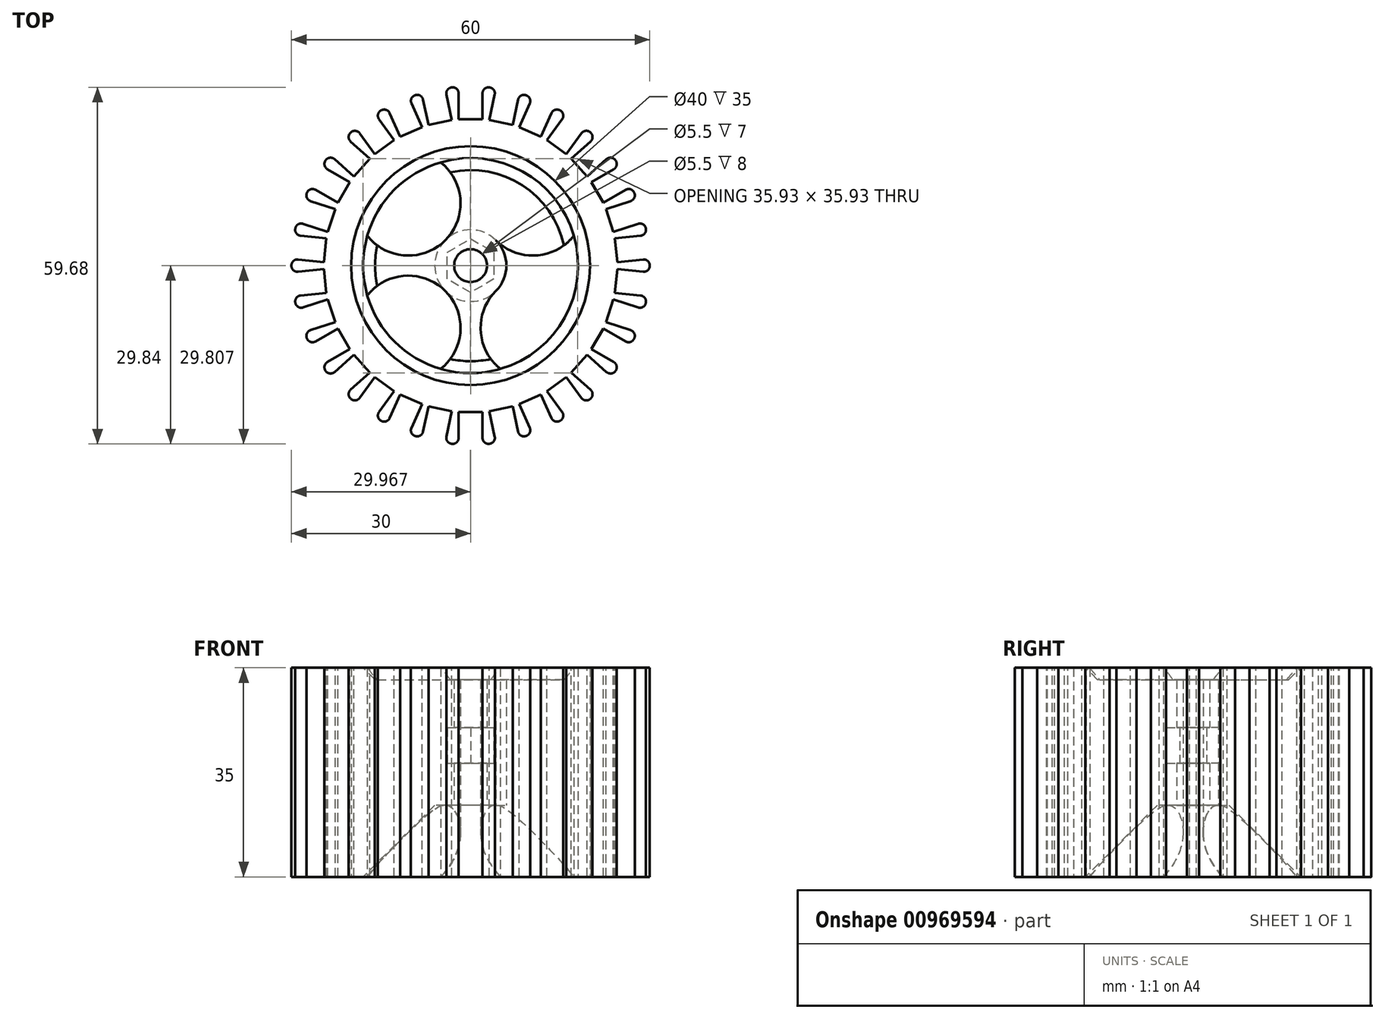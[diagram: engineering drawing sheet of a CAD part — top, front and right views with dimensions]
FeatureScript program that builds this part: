
annotation { "Feature Type Name" : "Feature", "Feature Type Description" : "" }
export const myFeature = defineFeature(function(context is Context, id is Id, definition is map)
    precondition{}
    {
        {
            var Q0;
            Q0=qCreatedBy(makeId("Top.planeOp"),FACE);
            var sketch = newSketch(context, id + "F0", { "sketchPlane" : qUnion([Q0])});
            skCircle(sketch, "E0", {"center": v(0, 0) * mm, "radius": 30 * mm});
            skCircle(sketch, "E1", {"center": v(0, 0) * mm, "radius": 20 * mm});
            skCircle(sketch, "E2", {"center": v(0, 0) * mm, "radius": 21 * mm});
            skCircle(sketch, "E3", {"center": v(0, 0) * mm, "radius": 18 * mm});
            skCircle(sketch, "E4", {"center": v(0, 0) * mm, "radius": 6 * mm});
            skArc(sketch, "E5", {"start": v(-17.3, 5) * mm, "mid": v(-4.24, 4.24) * mm, "end": v(-5, 17.3) * mm});
            skArc(sketch, "E6.MirrorCS", {"start": v(17.3, 5) * mm, "mid": v(4.24, 4.24) * mm, "end": v(5, 17.3) * mm});
            skArc(sketch, "E7.MirrorCS", {"start": v(-17.3, -5) * mm, "mid": v(-4.24, -4.24) * mm, "end": v(-5, -17.3) * mm});
            skArc(sketch, "E8.MirrorCS", {"start": v(17.3, -5) * mm, "mid": v(4.24, -4.24) * mm, "end": v(5, -17.3) * mm});
            skCircle(sketch, "E9.cCircle", {"center": v(0, 0) * mm, "radius": 3.9 * mm, "construction": true});
            skLineSegment(sketch, "E9.0", {"start": v(3.9, 2.25) * mm, "end": v(3.9, -2.25) * mm});
            skLineSegment(sketch, "E9.1", {"start": v(3.9, -2.25) * mm, "end": v(0, -4.5) * mm});
            skLineSegment(sketch, "E9.2", {"start": v(0, -4.5) * mm, "end": v(-3.9, -2.25) * mm});
            skLineSegment(sketch, "E9.3", {"start": v(-3.9, -2.25) * mm, "end": v(-3.9, 2.25) * mm});
            skLineSegment(sketch, "E9.4", {"start": v(-3.9, 2.25) * mm, "end": v(0, 4.5) * mm});
            skLineSegment(sketch, "E9.5", {"start": v(0, 4.5) * mm, "end": v(3.9, 2.25) * mm});
            skPoint(sketch, "E9.0.midPoint", {"position": v(3.9, 0) * mm});
            skCircle(sketch, "E10", {"center": v(0, 0) * mm, "radius": 3 * mm});
            skCircle(sketch, "E11", {"center": v(0, 0) * mm, "radius": 2.75 * mm});
            skSolve(sketch);
        }
        {
            var Q0;
            {var subQ0=sQuery(id+"F0.wireOp",EDGE,"E5");var subQ1=sQuery(id+"F0.wireOp",EDGE,"E3");var subQ2=makeQuery(id+"F0.imprint","INTERSECT",VERTEX,{"disambiguationData":[OD(1.0)],"derivedFrom":[subQ1,subQ0]});Q0=makeQuery(id+"F0.imprint","IMPRINT",FACE,{"disambiguationData":[TD([[makeQuery(id+"F0.imprint","IMPRINT",EDGE,{"disambiguationData":[TD([[subQ2,1.0]])],"derivedFrom":subQ1}),1.0]])]});}
            var Q1;
            {var subQ0=sQuery(id+"F0.wireOp",EDGE,"E5");var subQ1=sQuery(id+"F0.wireOp",EDGE,"E3");var subQ2=makeQuery(id+"F0.imprint","INTERSECT",VERTEX,{"disambiguationData":[OD(0.0)],"derivedFrom":[subQ1,subQ0]});Q1=makeQuery(id+"F0.imprint","IMPRINT",FACE,{"disambiguationData":[TD([[makeQuery(id+"F0.imprint","IMPRINT",EDGE,{"disambiguationData":[TD([[subQ2,-1.0]])],"derivedFrom":subQ1}),1.0]])]});}
            var Q2;
            {var subQ0=sQuery(id+"F0.wireOp",EDGE,"E7.MirrorCS");var subQ1=sQuery(id+"F0.wireOp",EDGE,"E3");var subQ2=makeQuery(id+"F0.imprint","INTERSECT",VERTEX,{"disambiguationData":[OD(1.0)],"derivedFrom":[subQ1,subQ0]});Q2=makeQuery(id+"F0.imprint","IMPRINT",FACE,{"disambiguationData":[TD([[makeQuery(id+"F0.imprint","IMPRINT",EDGE,{"disambiguationData":[TD([[subQ2,-1.0]])],"derivedFrom":subQ1}),1.0]])]});}
            var Q3;
            {var subQ0=sQuery(id+"F0.wireOp",EDGE,"E6.MirrorCS");var subQ1=sQuery(id+"F0.wireOp",EDGE,"E3");var subQ2=makeQuery(id+"F0.imprint","INTERSECT",VERTEX,{"disambiguationData":[OD(0.0)],"derivedFrom":[subQ1,subQ0]});Q3=makeQuery(id+"F0.imprint","IMPRINT",FACE,{"disambiguationData":[TD([[makeQuery(id+"F0.imprint","IMPRINT",EDGE,{"disambiguationData":[TD([[subQ2,1.0]])],"derivedFrom":subQ1}),1.0]])]});}
            var Q4;
            Q4=makeQuery(id+"F0.imprint","IMPRINT",FACE,{"disambiguationData":[TD([[makeQuery(id+"F0.imprint","IMPRINT",EDGE,{"derivedFrom":sQuery(id+"F0.wireOp",EDGE,"E1")}),1.0]])]});
            var Q5;
            Q5=makeQuery(id+"F0.imprint","IMPRINT",FACE,{"disambiguationData":[TD([[makeQuery(id+"F0.imprint","IMPRINT",EDGE,{"derivedFrom":sQuery(id+"F0.wireOp",EDGE,"E9.0")}),1.0]])]});
            var Q6;
            Q6=makeQuery(id+"F0.imprint","IMPRINT",FACE,{"disambiguationData":[TD([[makeQuery(id+"F0.imprint","IMPRINT",EDGE,{"derivedFrom":sQuery(id+"F0.wireOp",EDGE,"E9.0")}),-1.0]])]});
            extrude(context, id + "F1", {"entities" : qUnion([Q0, Q1, Q2, Q3, Q4, Q5, Q6]), "depth" : 35 * mm, "offsetDistance" : 25 * mm});
        }
        {
            var Q0;
            Q0=makeQuery(id+"F0.imprint","IMPRINT",FACE,{"disambiguationData":[TD([[makeQuery(id+"F0.imprint","IMPRINT",EDGE,{"derivedFrom":sQuery(id+"F0.wireOp",EDGE,"E0")}),1.0]])]});
            var Q1;
            Q1=makeQuery(id+"F0.imprint","IMPRINT",FACE,{"disambiguationData":[TD([[makeQuery(id+"F0.imprint","IMPRINT",EDGE,{"derivedFrom":sQuery(id+"F0.wireOp",EDGE,"E1")}),-1.0]])]});
            extrude(context, id + "F2", {"entities" : qUnion([Q0, Q1]), "depth" : 35 * mm, "offsetDistance" : 25 * mm});
        }
        {
            var Q0;
            Q0=makeQuery(id+"F0.imprint","IMPRINT",FACE,{"disambiguationData":[TD([[makeQuery(id+"F0.imprint","IMPRINT",EDGE,{"derivedFrom":sQuery(id+"F0.wireOp",EDGE,"E10")}),1.0]])]});
            extrude(context, id + "F3", {"entities" : qUnion([Q0]), "operationType" : NewBodyOperationType.ADD, "depth" : 33 * mm, "offsetDistance" : 25 * mm, "hasSecondDirection" : true, "secondDirectionOppositeDirection" : true, "secondDirectionDepth" : -12 * mm});
        }
        {
            var Q0;
            Q0=makeQuery(id+"F1.opExtrude","CAP_EDGE",EDGE,{"disambiguationData":[OSD([sQuery(id+"F0.wireOp",EDGE,"E10")])],"isStart":true});
            var Q1;
            Q1=makeQuery(id+"F1.opExtrude","CAP_EDGE",EDGE,{"disambiguationData":[OSD([sQuery(id+"F0.wireOp",EDGE,"E10")])],"isStart":false});
            chamfer(context, id + "F4", {"entities" : qUnion([Q0, Q1]), "width" : 15 * mm, "tangentPropagation" : true});
        }
        {
            var Q0;
            Q0=qCreatedBy(makeId("Front.planeOp"),FACE);
            cPlane(context, id + "F5", {"entities" : qUnion([Q0]), "cplaneType" : CPlaneType.OFFSET, "offset" : (32.5 - 5) * mm, "width" : 150 * mm, "height" : 150 * mm});
        }
        {
            var Q0;
            Q0=qCreatedBy(id+"F5.planeOp",FACE);
            var sketch = newSketch(context, id + "F6", { "sketchPlane" : qUnion([Q0])});
            skLineSegment(sketch, "E12.bottom", {"start": v(-2, 0) * mm, "end": v(2, 0) * mm});
            skLineSegment(sketch, "E12.top", {"start": v(-2, 35) * mm, "end": v(2, 35) * mm});
            skLineSegment(sketch, "E12.left", {"start": v(-2, 0) * mm, "end": v(-2, 35) * mm});
            skLineSegment(sketch, "E12.right", {"start": v(2, 0) * mm, "end": v(2, 35) * mm});
            skSolve(sketch);
        }
        {
            var Q0;
            Q0=makeQuery(id+"F6.imprint","IMPRINT",FACE,{"disambiguationData":[TD([[makeQuery(id+"F6.imprint","IMPRINT",EDGE,{"derivedFrom":sQuery(id+"F6.wireOp",EDGE,"E12.bottom")}),1.0]])]});
            extrude(context, id + "F7", {"entities" : qUnion([Q0]), "oppositeDirection" : true, "depth" : 3 * mm, "offsetDistance" : 25 * mm, "hasSecondDirection" : true, "secondDirectionOppositeDirection" : false, "secondDirectionDepth" : 2.5 * mm});
        }
        {
            var Q0;
            Q0=makeQuery(id+"F7.opExtrude","SWEPT_BODY",BODY,{"disambiguationData":[OSD([sQuery(id+"F6.wireOp",EDGE,"E12.bottom"),sQuery(id+"F6.wireOp",EDGE,"E12.top"),sQuery(id+"F6.wireOp",EDGE,"E12.left"),sQuery(id+"F6.wireOp",EDGE,"E12.right")])]});
            var Q1;
            Q1=makeQuery(id+"F3.opExtrude","CAP_EDGE",EDGE,{"disambiguationData":[OSD([sQuery(id+"F0.wireOp",EDGE,"E11")])],"isStart":false});
            circularPattern(context, id + "F8", {"operationType" : NewBodyOperationType.REMOVE, "entities" : qUnion([Q0]), "axis" : qUnion([Q1]), "angle" : 360 * degree, "instanceCount" : 30, "equalSpace" : true});
        }
        {
            var Q0;
            Q0=makeQuery(id+"F0.imprint","IMPRINT",FACE,{"disambiguationData":[TD([[makeQuery(id+"F0.imprint","IMPRINT",EDGE,{"derivedFrom":sQuery(id+"F0.wireOp",EDGE,"E10")}),1.0]])]});
            var Q1;
            Q1=makeQuery(id+"F0.imprint","IMPRINT",FACE,{"disambiguationData":[TD([[makeQuery(id+"F0.imprint","IMPRINT",EDGE,{"derivedFrom":sQuery(id+"F0.wireOp",EDGE,"E9.0")}),-1.0]])]});
            extrude(context, id + "F9", {"entities" : qUnion([Q0, Q1]), "operationType" : NewBodyOperationType.REMOVE, "depth" : 6 * mm, "offsetDistance" : 25 * mm});
        }
        {
            var Q0;
            Q0=makeQuery(id+"F0.imprint","IMPRINT",FACE,{"disambiguationData":[TD([[makeQuery(id+"F0.imprint","IMPRINT",EDGE,{"derivedFrom":sQuery(id+"F0.wireOp",EDGE,"E9.0")}),-1.0]])]});
            var Q1;
            Q1=makeQuery(id+"F0.imprint","IMPRINT",FACE,{"disambiguationData":[TD([[makeQuery(id+"F0.imprint","IMPRINT",EDGE,{"derivedFrom":sQuery(id+"F0.wireOp",EDGE,"E10")}),1.0]])]});
            extrude(context, id + "F10", {"entities" : qUnion([Q0, Q1]), "operationType" : NewBodyOperationType.REMOVE, "depth" : 25 * mm, "offsetDistance" : 25 * mm, "hasSecondDirection" : true, "secondDirectionOppositeDirection" : false, "secondDirectionDepth" : 19 * mm});
        }
        {
            var Q0;
            Q0=makeQuery(id+"F8.boolean.opBoolean","INTERSECT",EDGE,{"derivedFrom":[makeQuery(id+"F2.opExtrude","SWEPT_FACE",FACE,{"disambiguationData":[OSD([sQuery(id+"F0.wireOp",EDGE,"E0")])]}),makeQuery(id+"F8.opPattern","COPY",FACE,{"derivedFrom":makeQuery(id+"F7.opExtrude","SWEPT_FACE",FACE,{"disambiguationData":[OSD([sQuery(id+"F6.wireOp",EDGE,"E12.right")])]}),"instanceName":"17"})]});
            var Q1;
            Q1=makeQuery(id+"F8.boolean.opBoolean","INTERSECT",EDGE,{"derivedFrom":[makeQuery(id+"F2.opExtrude","SWEPT_FACE",FACE,{"disambiguationData":[OSD([sQuery(id+"F0.wireOp",EDGE,"E0")])]}),makeQuery(id+"F8.opPattern","COPY",FACE,{"derivedFrom":makeQuery(id+"F7.opExtrude","SWEPT_FACE",FACE,{"disambiguationData":[OSD([sQuery(id+"F6.wireOp",EDGE,"E12.left")])]}),"instanceName":"18"})]});
            var Q2;
            Q2=makeQuery(id+"F8.boolean.opBoolean","INTERSECT",EDGE,{"derivedFrom":[makeQuery(id+"F2.opExtrude","SWEPT_FACE",FACE,{"disambiguationData":[OSD([sQuery(id+"F0.wireOp",EDGE,"E0")])]}),makeQuery(id+"F8.opPattern","COPY",FACE,{"derivedFrom":makeQuery(id+"F7.opExtrude","SWEPT_FACE",FACE,{"disambiguationData":[OSD([sQuery(id+"F6.wireOp",EDGE,"E12.right")])]}),"instanceName":"18"})]});
            var Q3;
            Q3=makeQuery(id+"F8.boolean.opBoolean","INTERSECT",EDGE,{"derivedFrom":[makeQuery(id+"F2.opExtrude","SWEPT_FACE",FACE,{"disambiguationData":[OSD([sQuery(id+"F0.wireOp",EDGE,"E0")])]}),makeQuery(id+"F8.opPattern","COPY",FACE,{"derivedFrom":makeQuery(id+"F7.opExtrude","SWEPT_FACE",FACE,{"disambiguationData":[OSD([sQuery(id+"F6.wireOp",EDGE,"E12.left")])]}),"instanceName":"19"})]});
            var Q4;
            Q4=makeQuery(id+"F8.boolean.opBoolean","INTERSECT",EDGE,{"derivedFrom":[makeQuery(id+"F2.opExtrude","SWEPT_FACE",FACE,{"disambiguationData":[OSD([sQuery(id+"F0.wireOp",EDGE,"E0")])]}),makeQuery(id+"F8.opPattern","COPY",FACE,{"derivedFrom":makeQuery(id+"F7.opExtrude","SWEPT_FACE",FACE,{"disambiguationData":[OSD([sQuery(id+"F6.wireOp",EDGE,"E12.right")])]}),"instanceName":"19"})]});
            var Q5;
            Q5=makeQuery(id+"F8.boolean.opBoolean","INTERSECT",EDGE,{"derivedFrom":[makeQuery(id+"F2.opExtrude","SWEPT_FACE",FACE,{"disambiguationData":[OSD([sQuery(id+"F0.wireOp",EDGE,"E0")])]}),makeQuery(id+"F8.opPattern","COPY",FACE,{"derivedFrom":makeQuery(id+"F7.opExtrude","SWEPT_FACE",FACE,{"disambiguationData":[OSD([sQuery(id+"F6.wireOp",EDGE,"E12.left")])]}),"instanceName":"20"})]});
            var Q6;
            Q6=makeQuery(id+"F8.boolean.opBoolean","INTERSECT",EDGE,{"derivedFrom":[makeQuery(id+"F2.opExtrude","SWEPT_FACE",FACE,{"disambiguationData":[OSD([sQuery(id+"F0.wireOp",EDGE,"E0")])]}),makeQuery(id+"F8.opPattern","COPY",FACE,{"derivedFrom":makeQuery(id+"F7.opExtrude","SWEPT_FACE",FACE,{"disambiguationData":[OSD([sQuery(id+"F6.wireOp",EDGE,"E12.right")])]}),"instanceName":"20"})]});
            var Q7;
            Q7=makeQuery(id+"F8.boolean.opBoolean","INTERSECT",EDGE,{"derivedFrom":[makeQuery(id+"F2.opExtrude","SWEPT_FACE",FACE,{"disambiguationData":[OSD([sQuery(id+"F0.wireOp",EDGE,"E0")])]}),makeQuery(id+"F8.opPattern","COPY",FACE,{"derivedFrom":makeQuery(id+"F7.opExtrude","SWEPT_FACE",FACE,{"disambiguationData":[OSD([sQuery(id+"F6.wireOp",EDGE,"E12.left")])]}),"instanceName":"21"})]});
            var Q8;
            Q8=makeQuery(id+"F8.boolean.opBoolean","INTERSECT",EDGE,{"derivedFrom":[makeQuery(id+"F2.opExtrude","SWEPT_FACE",FACE,{"disambiguationData":[OSD([sQuery(id+"F0.wireOp",EDGE,"E0")])]}),makeQuery(id+"F8.opPattern","COPY",FACE,{"derivedFrom":makeQuery(id+"F7.opExtrude","SWEPT_FACE",FACE,{"disambiguationData":[OSD([sQuery(id+"F6.wireOp",EDGE,"E12.right")])]}),"instanceName":"21"})]});
            var Q9;
            Q9=makeQuery(id+"F8.boolean.opBoolean","INTERSECT",EDGE,{"derivedFrom":[makeQuery(id+"F2.opExtrude","SWEPT_FACE",FACE,{"disambiguationData":[OSD([sQuery(id+"F0.wireOp",EDGE,"E0")])]}),makeQuery(id+"F8.opPattern","COPY",FACE,{"derivedFrom":makeQuery(id+"F7.opExtrude","SWEPT_FACE",FACE,{"disambiguationData":[OSD([sQuery(id+"F6.wireOp",EDGE,"E12.left")])]}),"instanceName":"22"})]});
            var Q10;
            Q10=makeQuery(id+"F8.boolean.opBoolean","INTERSECT",EDGE,{"derivedFrom":[makeQuery(id+"F2.opExtrude","SWEPT_FACE",FACE,{"disambiguationData":[OSD([sQuery(id+"F0.wireOp",EDGE,"E0")])]}),makeQuery(id+"F8.opPattern","COPY",FACE,{"derivedFrom":makeQuery(id+"F7.opExtrude","SWEPT_FACE",FACE,{"disambiguationData":[OSD([sQuery(id+"F6.wireOp",EDGE,"E12.right")])]}),"instanceName":"22"})]});
            var Q11;
            Q11=makeQuery(id+"F8.boolean.opBoolean","INTERSECT",EDGE,{"derivedFrom":[makeQuery(id+"F2.opExtrude","SWEPT_FACE",FACE,{"disambiguationData":[OSD([sQuery(id+"F0.wireOp",EDGE,"E0")])]}),makeQuery(id+"F8.opPattern","COPY",FACE,{"derivedFrom":makeQuery(id+"F7.opExtrude","SWEPT_FACE",FACE,{"disambiguationData":[OSD([sQuery(id+"F6.wireOp",EDGE,"E12.left")])]}),"instanceName":"23"})]});
            var Q12;
            Q12=makeQuery(id+"F8.boolean.opBoolean","INTERSECT",EDGE,{"derivedFrom":[makeQuery(id+"F2.opExtrude","SWEPT_FACE",FACE,{"disambiguationData":[OSD([sQuery(id+"F0.wireOp",EDGE,"E0")])]}),makeQuery(id+"F8.opPattern","COPY",FACE,{"derivedFrom":makeQuery(id+"F7.opExtrude","SWEPT_FACE",FACE,{"disambiguationData":[OSD([sQuery(id+"F6.wireOp",EDGE,"E12.right")])]}),"instanceName":"23"})]});
            var Q13;
            Q13=makeQuery(id+"F8.boolean.opBoolean","INTERSECT",EDGE,{"derivedFrom":[makeQuery(id+"F2.opExtrude","SWEPT_FACE",FACE,{"disambiguationData":[OSD([sQuery(id+"F0.wireOp",EDGE,"E0")])]}),makeQuery(id+"F8.opPattern","COPY",FACE,{"derivedFrom":makeQuery(id+"F7.opExtrude","SWEPT_FACE",FACE,{"disambiguationData":[OSD([sQuery(id+"F6.wireOp",EDGE,"E12.left")])]}),"instanceName":"24"})]});
            var Q14;
            Q14=makeQuery(id+"F8.boolean.opBoolean","INTERSECT",EDGE,{"derivedFrom":[makeQuery(id+"F2.opExtrude","SWEPT_FACE",FACE,{"disambiguationData":[OSD([sQuery(id+"F0.wireOp",EDGE,"E0")])]}),makeQuery(id+"F8.opPattern","COPY",FACE,{"derivedFrom":makeQuery(id+"F7.opExtrude","SWEPT_FACE",FACE,{"disambiguationData":[OSD([sQuery(id+"F6.wireOp",EDGE,"E12.right")])]}),"instanceName":"24"})]});
            var Q15;
            Q15=makeQuery(id+"F8.boolean.opBoolean","INTERSECT",EDGE,{"derivedFrom":[makeQuery(id+"F2.opExtrude","SWEPT_FACE",FACE,{"disambiguationData":[OSD([sQuery(id+"F0.wireOp",EDGE,"E0")])]}),makeQuery(id+"F8.opPattern","COPY",FACE,{"derivedFrom":makeQuery(id+"F7.opExtrude","SWEPT_FACE",FACE,{"disambiguationData":[OSD([sQuery(id+"F6.wireOp",EDGE,"E12.left")])]}),"instanceName":"25"})]});
            var Q16;
            Q16=makeQuery(id+"F8.boolean.opBoolean","INTERSECT",EDGE,{"derivedFrom":[makeQuery(id+"F2.opExtrude","SWEPT_FACE",FACE,{"disambiguationData":[OSD([sQuery(id+"F0.wireOp",EDGE,"E0")])]}),makeQuery(id+"F8.opPattern","COPY",FACE,{"derivedFrom":makeQuery(id+"F7.opExtrude","SWEPT_FACE",FACE,{"disambiguationData":[OSD([sQuery(id+"F6.wireOp",EDGE,"E12.right")])]}),"instanceName":"25"})]});
            var Q17;
            Q17=makeQuery(id+"F8.boolean.opBoolean","INTERSECT",EDGE,{"derivedFrom":[makeQuery(id+"F2.opExtrude","SWEPT_FACE",FACE,{"disambiguationData":[OSD([sQuery(id+"F0.wireOp",EDGE,"E0")])]}),makeQuery(id+"F8.opPattern","COPY",FACE,{"derivedFrom":makeQuery(id+"F7.opExtrude","SWEPT_FACE",FACE,{"disambiguationData":[OSD([sQuery(id+"F6.wireOp",EDGE,"E12.left")])]}),"instanceName":"26"})]});
            var Q18;
            Q18=makeQuery(id+"F8.boolean.opBoolean","INTERSECT",EDGE,{"derivedFrom":[makeQuery(id+"F2.opExtrude","SWEPT_FACE",FACE,{"disambiguationData":[OSD([sQuery(id+"F0.wireOp",EDGE,"E0")])]}),makeQuery(id+"F8.opPattern","COPY",FACE,{"derivedFrom":makeQuery(id+"F7.opExtrude","SWEPT_FACE",FACE,{"disambiguationData":[OSD([sQuery(id+"F6.wireOp",EDGE,"E12.right")])]}),"instanceName":"26"})]});
            var Q19;
            Q19=makeQuery(id+"F8.boolean.opBoolean","INTERSECT",EDGE,{"derivedFrom":[makeQuery(id+"F2.opExtrude","SWEPT_FACE",FACE,{"disambiguationData":[OSD([sQuery(id+"F0.wireOp",EDGE,"E0")])]}),makeQuery(id+"F8.opPattern","COPY",FACE,{"derivedFrom":makeQuery(id+"F7.opExtrude","SWEPT_FACE",FACE,{"disambiguationData":[OSD([sQuery(id+"F6.wireOp",EDGE,"E12.left")])]}),"instanceName":"27"})]});
            var Q20;
            Q20=makeQuery(id+"F8.boolean.opBoolean","INTERSECT",EDGE,{"derivedFrom":[makeQuery(id+"F2.opExtrude","SWEPT_FACE",FACE,{"disambiguationData":[OSD([sQuery(id+"F0.wireOp",EDGE,"E0")])]}),makeQuery(id+"F8.opPattern","COPY",FACE,{"derivedFrom":makeQuery(id+"F7.opExtrude","SWEPT_FACE",FACE,{"disambiguationData":[OSD([sQuery(id+"F6.wireOp",EDGE,"E12.right")])]}),"instanceName":"27"})]});
            var Q21;
            Q21=makeQuery(id+"F8.boolean.opBoolean","INTERSECT",EDGE,{"derivedFrom":[makeQuery(id+"F2.opExtrude","SWEPT_FACE",FACE,{"disambiguationData":[OSD([sQuery(id+"F0.wireOp",EDGE,"E0")])]}),makeQuery(id+"F8.opPattern","COPY",FACE,{"derivedFrom":makeQuery(id+"F7.opExtrude","SWEPT_FACE",FACE,{"disambiguationData":[OSD([sQuery(id+"F6.wireOp",EDGE,"E12.left")])]}),"instanceName":"28"})]});
            var Q22;
            Q22=makeQuery(id+"F8.boolean.opBoolean","INTERSECT",EDGE,{"derivedFrom":[makeQuery(id+"F2.opExtrude","SWEPT_FACE",FACE,{"disambiguationData":[OSD([sQuery(id+"F0.wireOp",EDGE,"E0")])]}),makeQuery(id+"F8.opPattern","COPY",FACE,{"derivedFrom":makeQuery(id+"F7.opExtrude","SWEPT_FACE",FACE,{"disambiguationData":[OSD([sQuery(id+"F6.wireOp",EDGE,"E12.right")])]}),"instanceName":"28"})]});
            var Q23;
            Q23=makeQuery(id+"F8.boolean.opBoolean","INTERSECT",EDGE,{"derivedFrom":[makeQuery(id+"F2.opExtrude","SWEPT_FACE",FACE,{"disambiguationData":[OSD([sQuery(id+"F0.wireOp",EDGE,"E0")])]}),makeQuery(id+"F8.opPattern","COPY",FACE,{"derivedFrom":makeQuery(id+"F7.opExtrude","SWEPT_FACE",FACE,{"disambiguationData":[OSD([sQuery(id+"F6.wireOp",EDGE,"E12.left")])]}),"instanceName":"29"})]});
            var Q24;
            Q24=makeQuery(id+"F8.boolean.opBoolean","INTERSECT",EDGE,{"derivedFrom":[makeQuery(id+"F2.opExtrude","SWEPT_FACE",FACE,{"disambiguationData":[OSD([sQuery(id+"F0.wireOp",EDGE,"E0")])]}),makeQuery(id+"F8.opPattern","COPY",FACE,{"derivedFrom":makeQuery(id+"F7.opExtrude","SWEPT_FACE",FACE,{"disambiguationData":[OSD([sQuery(id+"F6.wireOp",EDGE,"E12.right")])]}),"instanceName":"29"})]});
            var Q25;
            Q25=makeQuery(id+"F8.boolean.opBoolean","INTERSECT",EDGE,{"derivedFrom":[makeQuery(id+"F2.opExtrude","SWEPT_FACE",FACE,{"disambiguationData":[OSD([sQuery(id+"F0.wireOp",EDGE,"E0")])]}),makeQuery(id+"F7.opExtrude","SWEPT_FACE",FACE,{"disambiguationData":[OSD([sQuery(id+"F6.wireOp",EDGE,"E12.left")])]})]});
            var Q26;
            Q26=makeQuery(id+"F8.boolean.opBoolean","INTERSECT",EDGE,{"derivedFrom":[makeQuery(id+"F2.opExtrude","SWEPT_FACE",FACE,{"disambiguationData":[OSD([sQuery(id+"F0.wireOp",EDGE,"E0")])]}),makeQuery(id+"F7.opExtrude","SWEPT_FACE",FACE,{"disambiguationData":[OSD([sQuery(id+"F6.wireOp",EDGE,"E12.right")])]})]});
            var Q27;
            Q27=makeQuery(id+"F8.boolean.opBoolean","INTERSECT",EDGE,{"derivedFrom":[makeQuery(id+"F2.opExtrude","SWEPT_FACE",FACE,{"disambiguationData":[OSD([sQuery(id+"F0.wireOp",EDGE,"E0")])]}),makeQuery(id+"F8.opPattern","COPY",FACE,{"derivedFrom":makeQuery(id+"F7.opExtrude","SWEPT_FACE",FACE,{"disambiguationData":[OSD([sQuery(id+"F6.wireOp",EDGE,"E12.left")])]}),"instanceName":"1"})]});
            var Q28;
            Q28=makeQuery(id+"F8.boolean.opBoolean","INTERSECT",EDGE,{"derivedFrom":[makeQuery(id+"F2.opExtrude","SWEPT_FACE",FACE,{"disambiguationData":[OSD([sQuery(id+"F0.wireOp",EDGE,"E0")])]}),makeQuery(id+"F8.opPattern","COPY",FACE,{"derivedFrom":makeQuery(id+"F7.opExtrude","SWEPT_FACE",FACE,{"disambiguationData":[OSD([sQuery(id+"F6.wireOp",EDGE,"E12.right")])]}),"instanceName":"1"})]});
            var Q29;
            Q29=makeQuery(id+"F8.boolean.opBoolean","INTERSECT",EDGE,{"derivedFrom":[makeQuery(id+"F2.opExtrude","SWEPT_FACE",FACE,{"disambiguationData":[OSD([sQuery(id+"F0.wireOp",EDGE,"E0")])]}),makeQuery(id+"F8.opPattern","COPY",FACE,{"derivedFrom":makeQuery(id+"F7.opExtrude","SWEPT_FACE",FACE,{"disambiguationData":[OSD([sQuery(id+"F6.wireOp",EDGE,"E12.left")])]}),"instanceName":"2"})]});
            var Q30;
            Q30=makeQuery(id+"F8.boolean.opBoolean","INTERSECT",EDGE,{"derivedFrom":[makeQuery(id+"F2.opExtrude","SWEPT_FACE",FACE,{"disambiguationData":[OSD([sQuery(id+"F0.wireOp",EDGE,"E0")])]}),makeQuery(id+"F8.opPattern","COPY",FACE,{"derivedFrom":makeQuery(id+"F7.opExtrude","SWEPT_FACE",FACE,{"disambiguationData":[OSD([sQuery(id+"F6.wireOp",EDGE,"E12.right")])]}),"instanceName":"2"})]});
            var Q31;
            Q31=makeQuery(id+"F8.boolean.opBoolean","INTERSECT",EDGE,{"derivedFrom":[makeQuery(id+"F2.opExtrude","SWEPT_FACE",FACE,{"disambiguationData":[OSD([sQuery(id+"F0.wireOp",EDGE,"E0")])]}),makeQuery(id+"F8.opPattern","COPY",FACE,{"derivedFrom":makeQuery(id+"F7.opExtrude","SWEPT_FACE",FACE,{"disambiguationData":[OSD([sQuery(id+"F6.wireOp",EDGE,"E12.left")])]}),"instanceName":"3"})]});
            var Q32;
            Q32=makeQuery(id+"F8.boolean.opBoolean","INTERSECT",EDGE,{"derivedFrom":[makeQuery(id+"F2.opExtrude","SWEPT_FACE",FACE,{"disambiguationData":[OSD([sQuery(id+"F0.wireOp",EDGE,"E0")])]}),makeQuery(id+"F8.opPattern","COPY",FACE,{"derivedFrom":makeQuery(id+"F7.opExtrude","SWEPT_FACE",FACE,{"disambiguationData":[OSD([sQuery(id+"F6.wireOp",EDGE,"E12.right")])]}),"instanceName":"3"})]});
            var Q33;
            Q33=makeQuery(id+"F8.boolean.opBoolean","INTERSECT",EDGE,{"derivedFrom":[makeQuery(id+"F2.opExtrude","SWEPT_FACE",FACE,{"disambiguationData":[OSD([sQuery(id+"F0.wireOp",EDGE,"E0")])]}),makeQuery(id+"F8.opPattern","COPY",FACE,{"derivedFrom":makeQuery(id+"F7.opExtrude","SWEPT_FACE",FACE,{"disambiguationData":[OSD([sQuery(id+"F6.wireOp",EDGE,"E12.left")])]}),"instanceName":"4"})]});
            var Q34;
            Q34=makeQuery(id+"F8.boolean.opBoolean","INTERSECT",EDGE,{"derivedFrom":[makeQuery(id+"F2.opExtrude","SWEPT_FACE",FACE,{"disambiguationData":[OSD([sQuery(id+"F0.wireOp",EDGE,"E0")])]}),makeQuery(id+"F8.opPattern","COPY",FACE,{"derivedFrom":makeQuery(id+"F7.opExtrude","SWEPT_FACE",FACE,{"disambiguationData":[OSD([sQuery(id+"F6.wireOp",EDGE,"E12.right")])]}),"instanceName":"4"})]});
            var Q35;
            Q35=makeQuery(id+"F8.boolean.opBoolean","INTERSECT",EDGE,{"derivedFrom":[makeQuery(id+"F2.opExtrude","SWEPT_FACE",FACE,{"disambiguationData":[OSD([sQuery(id+"F0.wireOp",EDGE,"E0")])]}),makeQuery(id+"F8.opPattern","COPY",FACE,{"derivedFrom":makeQuery(id+"F7.opExtrude","SWEPT_FACE",FACE,{"disambiguationData":[OSD([sQuery(id+"F6.wireOp",EDGE,"E12.left")])]}),"instanceName":"5"})]});
            var Q36;
            Q36=makeQuery(id+"F8.boolean.opBoolean","INTERSECT",EDGE,{"derivedFrom":[makeQuery(id+"F2.opExtrude","SWEPT_FACE",FACE,{"disambiguationData":[OSD([sQuery(id+"F0.wireOp",EDGE,"E0")])]}),makeQuery(id+"F8.opPattern","COPY",FACE,{"derivedFrom":makeQuery(id+"F7.opExtrude","SWEPT_FACE",FACE,{"disambiguationData":[OSD([sQuery(id+"F6.wireOp",EDGE,"E12.right")])]}),"instanceName":"5"})]});
            var Q37;
            Q37=makeQuery(id+"F8.boolean.opBoolean","INTERSECT",EDGE,{"derivedFrom":[makeQuery(id+"F2.opExtrude","SWEPT_FACE",FACE,{"disambiguationData":[OSD([sQuery(id+"F0.wireOp",EDGE,"E0")])]}),makeQuery(id+"F8.opPattern","COPY",FACE,{"derivedFrom":makeQuery(id+"F7.opExtrude","SWEPT_FACE",FACE,{"disambiguationData":[OSD([sQuery(id+"F6.wireOp",EDGE,"E12.left")])]}),"instanceName":"6"})]});
            var Q38;
            Q38=makeQuery(id+"F8.boolean.opBoolean","INTERSECT",EDGE,{"derivedFrom":[makeQuery(id+"F2.opExtrude","SWEPT_FACE",FACE,{"disambiguationData":[OSD([sQuery(id+"F0.wireOp",EDGE,"E0")])]}),makeQuery(id+"F8.opPattern","COPY",FACE,{"derivedFrom":makeQuery(id+"F7.opExtrude","SWEPT_FACE",FACE,{"disambiguationData":[OSD([sQuery(id+"F6.wireOp",EDGE,"E12.right")])]}),"instanceName":"6"})]});
            var Q39;
            Q39=makeQuery(id+"F8.boolean.opBoolean","INTERSECT",EDGE,{"derivedFrom":[makeQuery(id+"F2.opExtrude","SWEPT_FACE",FACE,{"disambiguationData":[OSD([sQuery(id+"F0.wireOp",EDGE,"E0")])]}),makeQuery(id+"F8.opPattern","COPY",FACE,{"derivedFrom":makeQuery(id+"F7.opExtrude","SWEPT_FACE",FACE,{"disambiguationData":[OSD([sQuery(id+"F6.wireOp",EDGE,"E12.left")])]}),"instanceName":"7"})]});
            var Q40;
            Q40=makeQuery(id+"F8.boolean.opBoolean","INTERSECT",EDGE,{"derivedFrom":[makeQuery(id+"F2.opExtrude","SWEPT_FACE",FACE,{"disambiguationData":[OSD([sQuery(id+"F0.wireOp",EDGE,"E0")])]}),makeQuery(id+"F8.opPattern","COPY",FACE,{"derivedFrom":makeQuery(id+"F7.opExtrude","SWEPT_FACE",FACE,{"disambiguationData":[OSD([sQuery(id+"F6.wireOp",EDGE,"E12.right")])]}),"instanceName":"7"})]});
            var Q41;
            Q41=makeQuery(id+"F8.boolean.opBoolean","INTERSECT",EDGE,{"derivedFrom":[makeQuery(id+"F2.opExtrude","SWEPT_FACE",FACE,{"disambiguationData":[OSD([sQuery(id+"F0.wireOp",EDGE,"E0")])]}),makeQuery(id+"F8.opPattern","COPY",FACE,{"derivedFrom":makeQuery(id+"F7.opExtrude","SWEPT_FACE",FACE,{"disambiguationData":[OSD([sQuery(id+"F6.wireOp",EDGE,"E12.left")])]}),"instanceName":"8"})]});
            var Q42;
            Q42=makeQuery(id+"F8.boolean.opBoolean","INTERSECT",EDGE,{"derivedFrom":[makeQuery(id+"F2.opExtrude","SWEPT_FACE",FACE,{"disambiguationData":[OSD([sQuery(id+"F0.wireOp",EDGE,"E0")])]}),makeQuery(id+"F8.opPattern","COPY",FACE,{"derivedFrom":makeQuery(id+"F7.opExtrude","SWEPT_FACE",FACE,{"disambiguationData":[OSD([sQuery(id+"F6.wireOp",EDGE,"E12.right")])]}),"instanceName":"8"})]});
            var Q43;
            Q43=makeQuery(id+"F8.boolean.opBoolean","INTERSECT",EDGE,{"derivedFrom":[makeQuery(id+"F2.opExtrude","SWEPT_FACE",FACE,{"disambiguationData":[OSD([sQuery(id+"F0.wireOp",EDGE,"E0")])]}),makeQuery(id+"F8.opPattern","COPY",FACE,{"derivedFrom":makeQuery(id+"F7.opExtrude","SWEPT_FACE",FACE,{"disambiguationData":[OSD([sQuery(id+"F6.wireOp",EDGE,"E12.left")])]}),"instanceName":"9"})]});
            var Q44;
            Q44=makeQuery(id+"F8.boolean.opBoolean","INTERSECT",EDGE,{"derivedFrom":[makeQuery(id+"F2.opExtrude","SWEPT_FACE",FACE,{"disambiguationData":[OSD([sQuery(id+"F0.wireOp",EDGE,"E0")])]}),makeQuery(id+"F8.opPattern","COPY",FACE,{"derivedFrom":makeQuery(id+"F7.opExtrude","SWEPT_FACE",FACE,{"disambiguationData":[OSD([sQuery(id+"F6.wireOp",EDGE,"E12.right")])]}),"instanceName":"9"})]});
            var Q45;
            Q45=makeQuery(id+"F8.boolean.opBoolean","INTERSECT",EDGE,{"derivedFrom":[makeQuery(id+"F2.opExtrude","SWEPT_FACE",FACE,{"disambiguationData":[OSD([sQuery(id+"F0.wireOp",EDGE,"E0")])]}),makeQuery(id+"F8.opPattern","COPY",FACE,{"derivedFrom":makeQuery(id+"F7.opExtrude","SWEPT_FACE",FACE,{"disambiguationData":[OSD([sQuery(id+"F6.wireOp",EDGE,"E12.left")])]}),"instanceName":"10"})]});
            var Q46;
            Q46=makeQuery(id+"F8.boolean.opBoolean","INTERSECT",EDGE,{"derivedFrom":[makeQuery(id+"F2.opExtrude","SWEPT_FACE",FACE,{"disambiguationData":[OSD([sQuery(id+"F0.wireOp",EDGE,"E0")])]}),makeQuery(id+"F8.opPattern","COPY",FACE,{"derivedFrom":makeQuery(id+"F7.opExtrude","SWEPT_FACE",FACE,{"disambiguationData":[OSD([sQuery(id+"F6.wireOp",EDGE,"E12.right")])]}),"instanceName":"10"})]});
            var Q47;
            Q47=makeQuery(id+"F8.boolean.opBoolean","INTERSECT",EDGE,{"derivedFrom":[makeQuery(id+"F2.opExtrude","SWEPT_FACE",FACE,{"disambiguationData":[OSD([sQuery(id+"F0.wireOp",EDGE,"E0")])]}),makeQuery(id+"F8.opPattern","COPY",FACE,{"derivedFrom":makeQuery(id+"F7.opExtrude","SWEPT_FACE",FACE,{"disambiguationData":[OSD([sQuery(id+"F6.wireOp",EDGE,"E12.left")])]}),"instanceName":"11"})]});
            var Q48;
            Q48=makeQuery(id+"F8.boolean.opBoolean","INTERSECT",EDGE,{"derivedFrom":[makeQuery(id+"F2.opExtrude","SWEPT_FACE",FACE,{"disambiguationData":[OSD([sQuery(id+"F0.wireOp",EDGE,"E0")])]}),makeQuery(id+"F8.opPattern","COPY",FACE,{"derivedFrom":makeQuery(id+"F7.opExtrude","SWEPT_FACE",FACE,{"disambiguationData":[OSD([sQuery(id+"F6.wireOp",EDGE,"E12.right")])]}),"instanceName":"11"})]});
            var Q49;
            Q49=makeQuery(id+"F8.boolean.opBoolean","INTERSECT",EDGE,{"derivedFrom":[makeQuery(id+"F2.opExtrude","SWEPT_FACE",FACE,{"disambiguationData":[OSD([sQuery(id+"F0.wireOp",EDGE,"E0")])]}),makeQuery(id+"F8.opPattern","COPY",FACE,{"derivedFrom":makeQuery(id+"F7.opExtrude","SWEPT_FACE",FACE,{"disambiguationData":[OSD([sQuery(id+"F6.wireOp",EDGE,"E12.left")])]}),"instanceName":"12"})]});
            var Q50;
            Q50=makeQuery(id+"F8.boolean.opBoolean","INTERSECT",EDGE,{"derivedFrom":[makeQuery(id+"F2.opExtrude","SWEPT_FACE",FACE,{"disambiguationData":[OSD([sQuery(id+"F0.wireOp",EDGE,"E0")])]}),makeQuery(id+"F8.opPattern","COPY",FACE,{"derivedFrom":makeQuery(id+"F7.opExtrude","SWEPT_FACE",FACE,{"disambiguationData":[OSD([sQuery(id+"F6.wireOp",EDGE,"E12.right")])]}),"instanceName":"12"})]});
            var Q51;
            Q51=makeQuery(id+"F8.boolean.opBoolean","INTERSECT",EDGE,{"derivedFrom":[makeQuery(id+"F2.opExtrude","SWEPT_FACE",FACE,{"disambiguationData":[OSD([sQuery(id+"F0.wireOp",EDGE,"E0")])]}),makeQuery(id+"F8.opPattern","COPY",FACE,{"derivedFrom":makeQuery(id+"F7.opExtrude","SWEPT_FACE",FACE,{"disambiguationData":[OSD([sQuery(id+"F6.wireOp",EDGE,"E12.left")])]}),"instanceName":"13"})]});
            var Q52;
            Q52=makeQuery(id+"F8.boolean.opBoolean","INTERSECT",EDGE,{"derivedFrom":[makeQuery(id+"F2.opExtrude","SWEPT_FACE",FACE,{"disambiguationData":[OSD([sQuery(id+"F0.wireOp",EDGE,"E0")])]}),makeQuery(id+"F8.opPattern","COPY",FACE,{"derivedFrom":makeQuery(id+"F7.opExtrude","SWEPT_FACE",FACE,{"disambiguationData":[OSD([sQuery(id+"F6.wireOp",EDGE,"E12.left")])]}),"instanceName":"17"})]});
            var Q53;
            Q53=makeQuery(id+"F8.boolean.opBoolean","INTERSECT",EDGE,{"derivedFrom":[makeQuery(id+"F2.opExtrude","SWEPT_FACE",FACE,{"disambiguationData":[OSD([sQuery(id+"F0.wireOp",EDGE,"E0")])]}),makeQuery(id+"F8.opPattern","COPY",FACE,{"derivedFrom":makeQuery(id+"F7.opExtrude","SWEPT_FACE",FACE,{"disambiguationData":[OSD([sQuery(id+"F6.wireOp",EDGE,"E12.right")])]}),"instanceName":"16"})]});
            var Q54;
            Q54=makeQuery(id+"F8.boolean.opBoolean","INTERSECT",EDGE,{"derivedFrom":[makeQuery(id+"F2.opExtrude","SWEPT_FACE",FACE,{"disambiguationData":[OSD([sQuery(id+"F0.wireOp",EDGE,"E0")])]}),makeQuery(id+"F8.opPattern","COPY",FACE,{"derivedFrom":makeQuery(id+"F7.opExtrude","SWEPT_FACE",FACE,{"disambiguationData":[OSD([sQuery(id+"F6.wireOp",EDGE,"E12.left")])]}),"instanceName":"16"})]});
            var Q55;
            Q55=makeQuery(id+"F8.boolean.opBoolean","INTERSECT",EDGE,{"derivedFrom":[makeQuery(id+"F2.opExtrude","SWEPT_FACE",FACE,{"disambiguationData":[OSD([sQuery(id+"F0.wireOp",EDGE,"E0")])]}),makeQuery(id+"F8.opPattern","COPY",FACE,{"derivedFrom":makeQuery(id+"F7.opExtrude","SWEPT_FACE",FACE,{"disambiguationData":[OSD([sQuery(id+"F6.wireOp",EDGE,"E12.right")])]}),"instanceName":"15"})]});
            var Q56;
            Q56=makeQuery(id+"F8.boolean.opBoolean","INTERSECT",EDGE,{"derivedFrom":[makeQuery(id+"F2.opExtrude","SWEPT_FACE",FACE,{"disambiguationData":[OSD([sQuery(id+"F0.wireOp",EDGE,"E0")])]}),makeQuery(id+"F8.opPattern","COPY",FACE,{"derivedFrom":makeQuery(id+"F7.opExtrude","SWEPT_FACE",FACE,{"disambiguationData":[OSD([sQuery(id+"F6.wireOp",EDGE,"E12.left")])]}),"instanceName":"15"})]});
            var Q57;
            Q57=makeQuery(id+"F8.boolean.opBoolean","INTERSECT",EDGE,{"derivedFrom":[makeQuery(id+"F2.opExtrude","SWEPT_FACE",FACE,{"disambiguationData":[OSD([sQuery(id+"F0.wireOp",EDGE,"E0")])]}),makeQuery(id+"F8.opPattern","COPY",FACE,{"derivedFrom":makeQuery(id+"F7.opExtrude","SWEPT_FACE",FACE,{"disambiguationData":[OSD([sQuery(id+"F6.wireOp",EDGE,"E12.right")])]}),"instanceName":"14"})]});
            var Q58;
            Q58=makeQuery(id+"F8.boolean.opBoolean","INTERSECT",EDGE,{"derivedFrom":[makeQuery(id+"F2.opExtrude","SWEPT_FACE",FACE,{"disambiguationData":[OSD([sQuery(id+"F0.wireOp",EDGE,"E0")])]}),makeQuery(id+"F8.opPattern","COPY",FACE,{"derivedFrom":makeQuery(id+"F7.opExtrude","SWEPT_FACE",FACE,{"disambiguationData":[OSD([sQuery(id+"F6.wireOp",EDGE,"E12.left")])]}),"instanceName":"14"})]});
            var Q59;
            Q59=makeQuery(id+"F8.boolean.opBoolean","INTERSECT",EDGE,{"derivedFrom":[makeQuery(id+"F2.opExtrude","SWEPT_FACE",FACE,{"disambiguationData":[OSD([sQuery(id+"F0.wireOp",EDGE,"E0")])]}),makeQuery(id+"F8.opPattern","COPY",FACE,{"derivedFrom":makeQuery(id+"F7.opExtrude","SWEPT_FACE",FACE,{"disambiguationData":[OSD([sQuery(id+"F6.wireOp",EDGE,"E12.right")])]}),"instanceName":"13"})]});
            fillet(context, id + "F11", {"entities" : qUnion([Q0, Q1, Q2, Q3, Q4, Q5, Q6, Q7, Q8, Q9, Q10, Q11, Q12, Q13, Q14, Q15, Q16, Q17, Q18, Q19, Q20, Q21, Q22, Q23, Q24, Q25, Q26, Q27, Q28, Q29, Q30, Q31, Q32, Q33, Q34, Q35, Q36, Q37, Q38, Q39, Q40, Q41, Q42, Q43, Q44, Q45, Q46, Q47, Q48, Q49, Q50, Q51, Q52, Q53, Q54, Q55, Q56, Q57, Q58, Q59]), "radius" : 1 * mm, "tangentPropagation" : true, "allowEdgeOverflow" : false});
        }
    });
